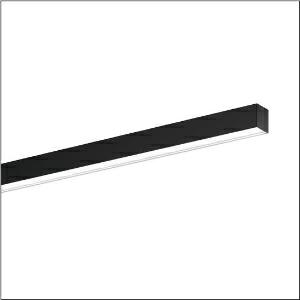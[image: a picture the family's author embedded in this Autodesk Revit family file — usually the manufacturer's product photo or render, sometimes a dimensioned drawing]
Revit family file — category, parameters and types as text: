
# Revit family: silica_r__21_51mx23db45bb_2d31
name_source: partatom
category: Lighting Fixtures
units: mm (PartAtom-declared; Revit-internal decimal feet)

## family parameters
Cut with Voids When Loaded = No
Host = Face
Light Source = No
Part Type = Normal
Room Calculation Point = No
Round Connector Dimension = Use Diameter
Shared = No

## types (1)
- --- (1 x LED, 4100 lm, 28.1 W, 4000K)
    Apparent Load = 28 VA
    CIE Flux Codes = 78 96 99 100 100
    Color Rendering = 80
    Color Temperature = 4000K
    Default Elevation = 1800 mm
    Description = Silica® 21, office luminaire, primary optical cover: prismatic diffuser, of PMMA, CAT 2 (L<= 3000cd/m²), light emission: direct distribution, primary light characteristic: symmetric, installation type: surface-mounted, LED, rated luminous flux: 4.100lm, luminous efficacy: 146lm/W, light colour: 840, colour temperature: 4000K, with terminal, 3+2-pole, max. 2.5mm², mains connection: 220..240V, AC, 50/60Hz, rated input power: 28.1W, luminaire housing, of aluminium, jet black (RAL 9005), length: 1.504mm, width: 53mm, height: 53mm, protection rating (complete): IP20, insulation class (complete): insulation class I (protective earthing), certification: CE, permissible operating ambient temperature: 0..+35°C, standard: EN 50419, packaging unit: 1 piece
    Height = 0 mm  [stored 0 ft]
    Lamp = 1 x LED
    Lamp Light Flux = 4100 lm
    Lamp Power = 28.1 W
    Lamp count = 1
    Length = 1504 mm
    Luminous efficacy = 146 lm/W
    Manufacturer = Siteco
    ModVariant = No
    Model = 51MX23DB45BB
    Mounting Place = Ceiling
    Mounting Type = Recessed
    Number of Poles = 1
    OnlyDefault = Yes
    Power Factor = 1
    Product Name = Silica® 21
    Product group = office luminaire | ceiling recessed
    ProductGroupID = 401
    Protection Class = Protection class I
    Protection Degree = IP 20
    RLX_Detail_Level = 1
    RLX_Emergency_Light_Flux = 0 lm
    RLX_Emergency_Type = 0
    RLX_Emergency_Type_DB = No
    RlxData = <blob elided: 23781 chars, md5=2f4bb380>
    Socket = socket
    Standby Power = 0 W
    System Light Flux = 4100 lm
    System Power = 28 W
    Type Comments = factory setting: luminous flux: 100 % | dim-lin: 254 | 323 mA
    Type Image = l_1313584.jpg
    URL = http://relux.com
    VarID = @adj_068107
    Voltage = 0 V
    Weight = 0.00 kg
    Width = 53 mm

note: [stored X ft] marks values corroborated as IEEE doubles in the binary element streams (Revit-internal decimal feet)

## geometry (parser evidence)
native form markers: Blend x4, Sweep x11
no freeform markers — native parametric forms only
